# Revit family: STAR
name_source: partatom
category: Generic Models
revit_build: Autodesk Revit Architecture 2015 (Build: 20141119_1515(x64)
units: mm (PartAtom-declared; Revit-internal decimal feet)

## types (16) — shared parameters
Default Elevation = 4' - 0"
Description = Vehicle Restraint
Manufacturer = Kelley Entrematic
Model = STAR
URL = http://kelleyentrematic.com

## per-type parameters (varying)
| type | Back Plate Height | Standoff |
| 27.5" Back Plate | 2' - 3 1/2" | 0' - 0 1/32" |
| 28.5" Back Plate | 2' - 4 1/2" | 0' - 0 1/32" |
| 29.5" Back Plate | 2' - 5 1/2" | 0' - 0 1/32" |
| 30.5" Back Plate | 2' - 6 1/2" | 0' - 0 1/32" |
| 30.5" Back Plate, 2" Standoff | 2' - 6 1/2" | 0' - 2" |
| 30.5" Back Plate, 12" Standoff | 2' - 6 1/2" | 1' - 0" |
| 30.5" Back Plate, 14" Standoff | 2' - 6 1/2" | 1' - 2" |
| 29.5" Back Plate, 2" Standoff | 2' - 5 1/2" | 0' - 2" |
| 29.5" Back Plate, 12" Standoff | 2' - 5 1/2" | 1' - 0" |
| 29.5" Back Plate, 14" Standoff | 2' - 5 1/2" | 1' - 2" |
| 28.5" Back Plate, 2" Standoff | 2' - 4 1/2" | 0' - 2" |
| 28.5" Back Plate, 12" Standoff | 2' - 4 1/2" | 1' - 0" |
| 28.5" Back Plate, 14" Standoff | 2' - 4 1/2" | 1' - 2" |
| 27.5" Back Plate, 2" Standoff | 2' - 3 1/2" | 0' - 2" |
| 27.5" Back Plate, 12" Standoff | 2' - 3 1/2" | 1' - 0" |
| 27.5" Back Plate, 14" Standoff | 2' - 3 1/2" | 1' - 2" |

## geometry (parser evidence)
native form markers: Blend x2, Sweep x6
no freeform markers — native parametric forms only
